# Revit family: 1333xxx Eclipse Round 350 - 2700K
name_source: partatom
category: Lighting Fixtures
units: mm (PartAtom-declared; Revit-internal decimal feet)

## family parameters
Always vertical = Yes
Cut with Voids When Loaded = No
Host = Wall
Light Source = Yes
OmniClass Number = 23.80.70.00
OmniClass Title = Lighting
Part Type = Normal
Room Calculation Point = No
Round Connector Dimension = Use Diameter
Shared = No

## types (1)
- CE
    ADA compliant = N / A
    Color Filter = 16777215
    Default Elevation = 0 mm  [stored 0 ft]
    Dimmable = No
    Dimming Lamp Color Temperature Shift = <None>
    Dimming Method = Not Applicable
    Driver Included = Yes
    Driver Required = No
    Efficacy (lm/w) = 41
    Electrical Class = 1
    Lamp = LED
    Length of Cable Supplied = Not Applicable
    Light Source Fixed = Yes
    Location / IP Rating = IP20
    Main Finish = Plaster
    Main Material = Plaster
    Manufacturer = Astro Lighting Ltd
    Manufacturer URL - Europe and Rest of World = www.astrolighting.com
    Manufacturer URL - North America = us.astrolighting.com
    Photometric Web File = 1333025_Eclipse Round 350 LED 2700K_Photometry_IES_Iss.01.ies
    Power (Watts) = 16.4
    Product CCT = 2700K
    Product CRI = 80
    Product Dimensions (MM) = Ø350 x 39
    Product Location = Wall
    Product Name = Eclipse Round 350
    Product SKU = 1333025
    Product Weight (KG) = 3.232
    Tilt Angle = 60.00°
    URL = www.astrolighting.com

note: [stored X ft] marks values corroborated as IEEE doubles in the binary element streams (Revit-internal decimal feet)

## geometry (parser evidence)
native form markers: Sweep x3
no freeform markers — native parametric forms only
